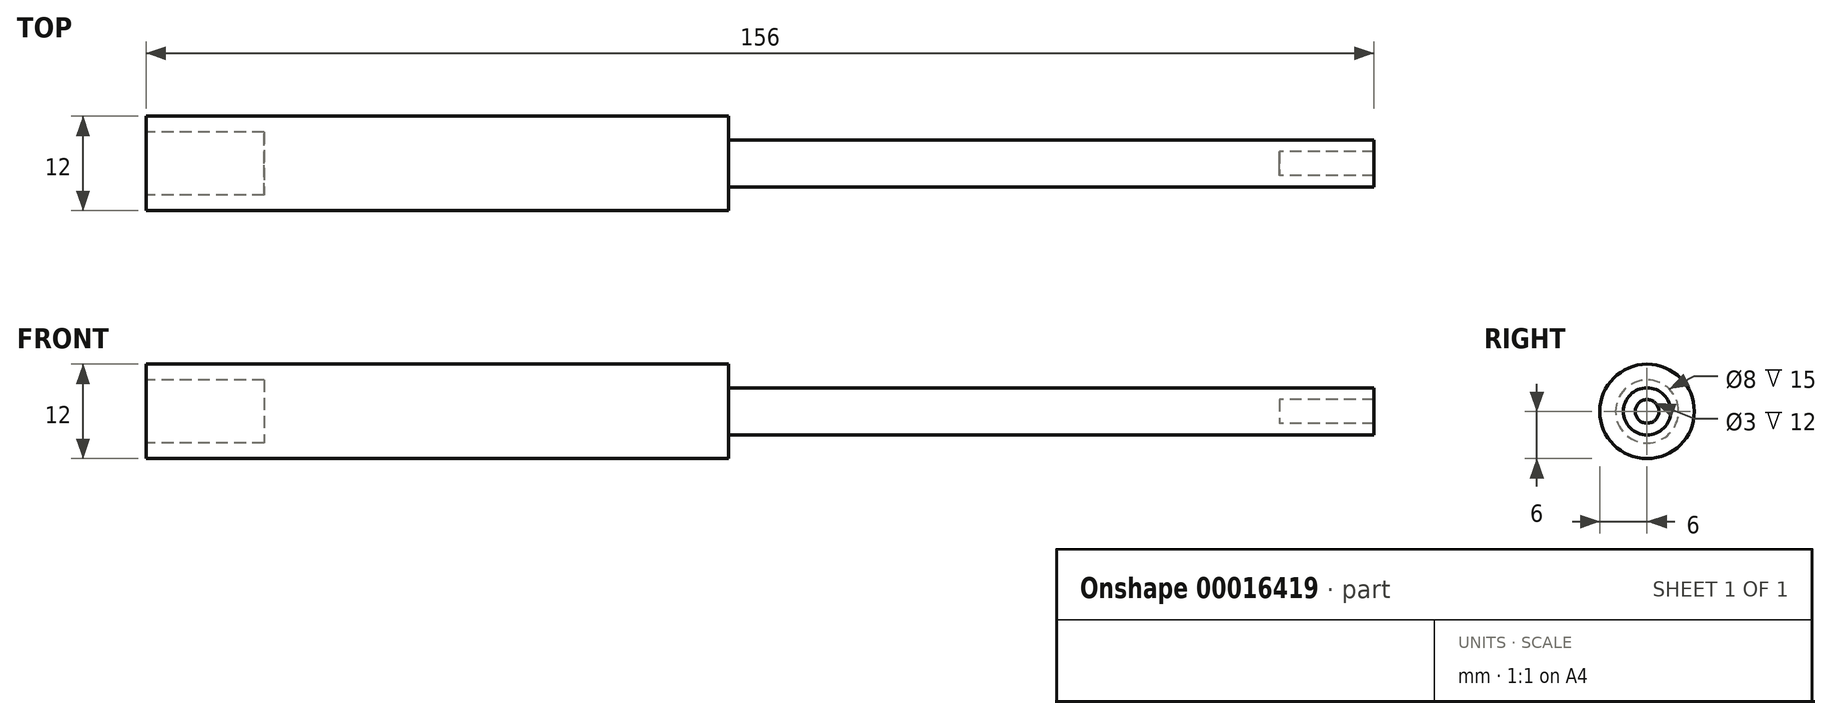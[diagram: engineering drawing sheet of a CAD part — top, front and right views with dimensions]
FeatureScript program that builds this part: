
annotation { "Feature Type Name" : "Feature", "Feature Type Description" : "" }
export const myFeature = defineFeature(function(context is Context, id is Id, definition is map)
    precondition{}
    {
        {
            var Q0;
            Q0=qCreatedBy(makeId("Front.planeOp"),FACE);
            var sketch = newSketch(context, id + "F0", { "sketchPlane" : qUnion([Q0])});
            skLineSegment(sketch, "E0.0", {"start": v(-23.51, 6) * mm, "end": v(50.49, 6) * mm});
            skLineSegment(sketch, "E1.0", {"start": v(-8.51, 0) * mm, "end": v(120.49, 0) * mm});
            skLineSegment(sketch, "E2.top", {"start": v(-8.51, 0) * mm, "end": v(50.49, 0) * mm});
            skLineSegment(sketch, "E2.left", {"start": v(-23.51, 6) * mm, "end": v(-23.51, 4) * mm});
            skLineSegment(sketch, "E2.right", {"start": v(50.49, 6) * mm, "end": v(50.49, 3) * mm});
            skLineSegment(sketch, "E3.0", {"start": v(132.49, 3) * mm, "end": v(132.49, 1.5) * mm});
            skLineSegment(sketch, "E4.0", {"start": v(50.49, 3) * mm, "end": v(132.49, 3) * mm});
            skLineSegment(sketch, "E5.0", {"start": v(120.49, 1.5) * mm, "end": v(132.49, 1.5) * mm});
            skLineSegment(sketch, "E6.0", {"start": v(120.49, 1.5) * mm, "end": v(120.49, 0) * mm});
            skLineSegment(sketch, "E7.0", {"start": v(-8.51, 4) * mm, "end": v(-8.51, 0) * mm});
            skLineSegment(sketch, "E8.0", {"start": v(-23.51, 4) * mm, "end": v(-8.51, 4) * mm});
            skPoint(sketch, "E9.orphan", {"position": v(132.49, 0) * mm});
            skPoint(sketch, "E10.orphan", {"position": v(-23.51, 0) * mm});
            skLineSegment(sketch, "E11", {"start": v(-23.51, 0) * mm, "end": v(132.49, 0) * mm, "construction": true});
            skSolve(sketch);
        }
        {
            var Q0;
            Q0=makeQuery(id+"F0.imprint","IMPRINT",FACE,{"disambiguationData":[TD([[makeQuery(id+"F0.imprint","IMPRINT",EDGE,{"derivedFrom":sQuery(id+"F0.wireOp",EDGE,"E1.0")}),1.0]])]});
            var Q1;
            Q1=sQuery(id+"F0.wireOp",EDGE,"E11");
            revolve(context, id + "F1", {"entities" : qUnion([Q0]), "axis" : qUnion([Q1]), "revolveType" : RevolveType.FULL});
        }
    });
